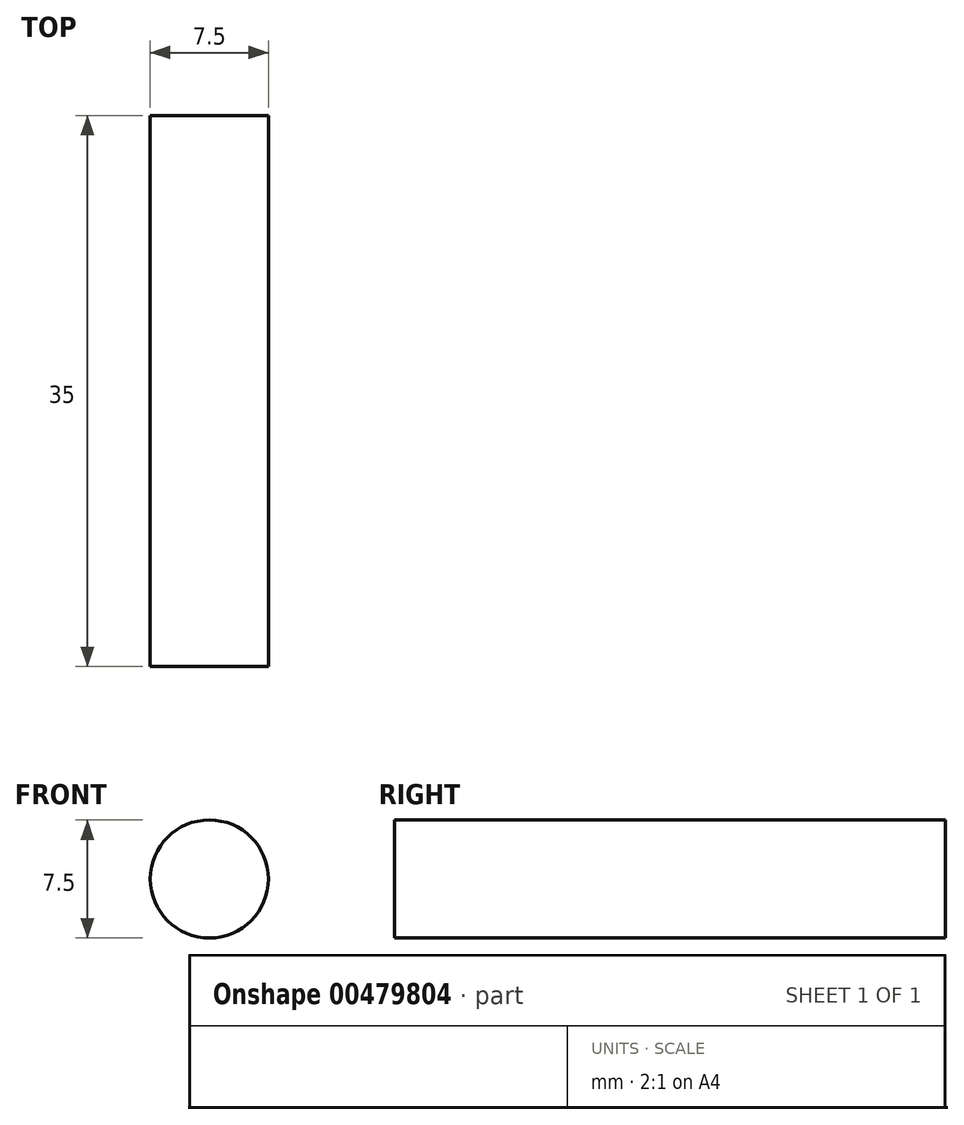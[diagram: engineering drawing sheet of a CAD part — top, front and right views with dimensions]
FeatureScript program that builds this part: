
annotation { "Feature Type Name" : "Feature", "Feature Type Description" : "" }
export const myFeature = defineFeature(function(context is Context, id is Id, definition is map)
    precondition{}
    {
        {
            var Q0;
            Q0=qCreatedBy(makeId("Front.planeOp"),FACE);
            var sketch = newSketch(context, id + "F0", { "sketchPlane" : qUnion([Q0])});
            skCircle(sketch, "E0", {"center": v(0, 0) * mm, "radius": 3.75 * mm});
            skSolve(sketch);
        }
        {
            var Q0;
            Q0=makeQuery(id+"F0.imprint","IMPRINT",FACE,{"disambiguationData":[TD([[makeQuery(id+"F0.imprint","IMPRINT",EDGE,{"derivedFrom":sQuery(id+"F0.wireOp",EDGE,"E0")}),1.0]])]});
            extrude(context, id + "F1", {"entities" : qUnion([Q0]), "depth" : 35 * mm});
        }
    });
